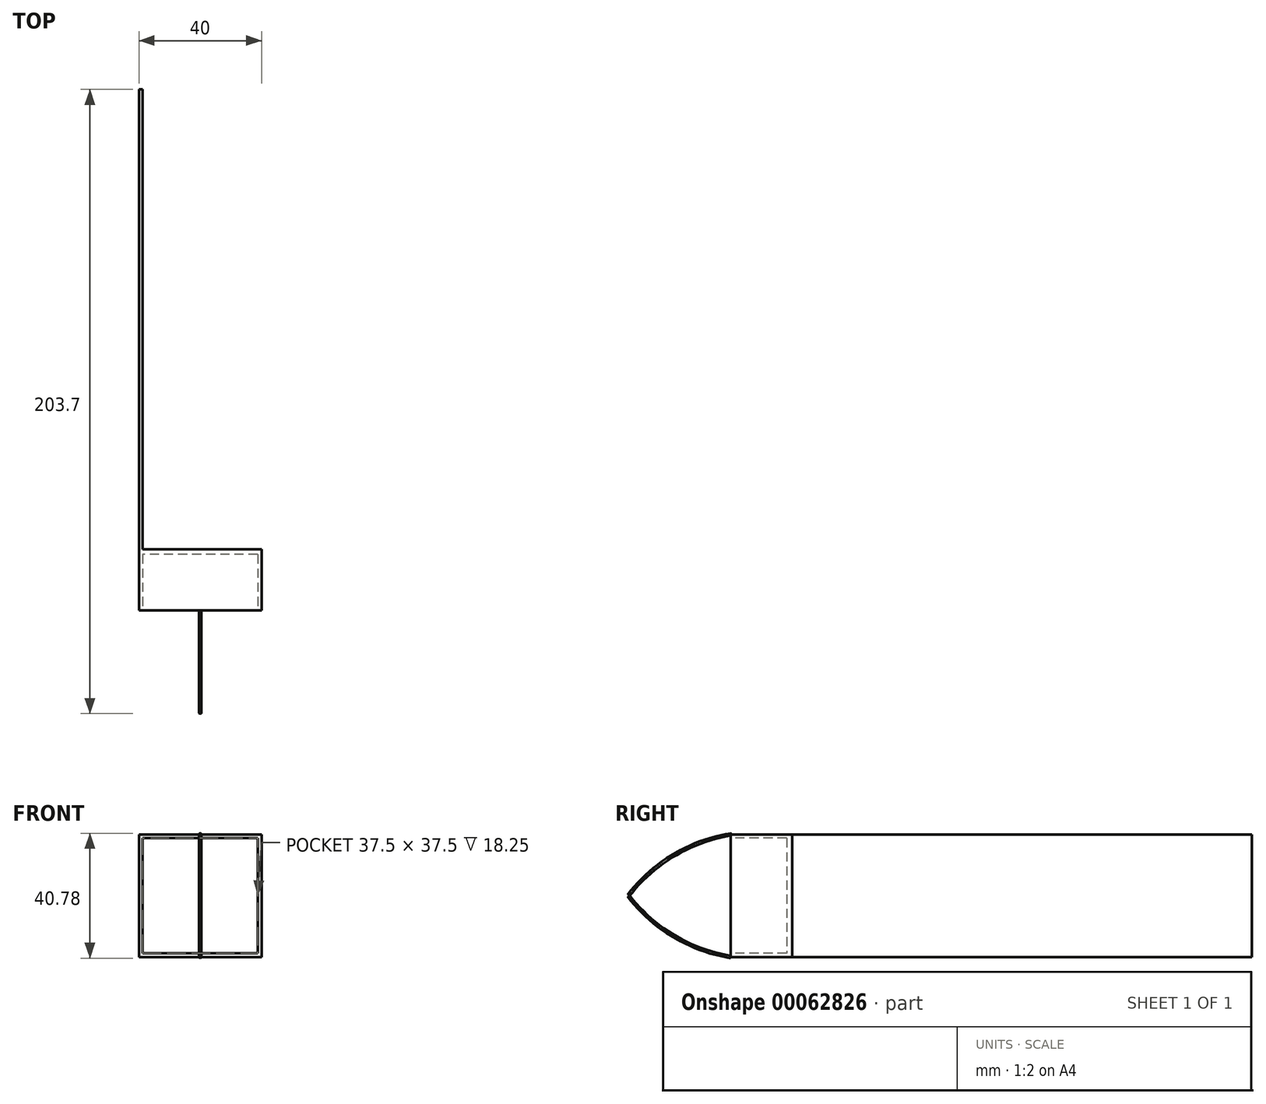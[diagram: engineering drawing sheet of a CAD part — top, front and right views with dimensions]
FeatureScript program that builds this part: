
annotation { "Feature Type Name" : "Feature", "Feature Type Description" : "" }
export const myFeature = defineFeature(function(context is Context, id is Id, definition is map)
    precondition{}
    {
        {
            var Q0;
            Q0=qCreatedBy(makeId("Front.planeOp"),FACE);
            var sketch = newSketch(context, id + "F0", { "sketchPlane" : qUnion([Q0])});
            skLineSegment(sketch, "E0.rect.bottom", {"start": v(20, 20) * mm, "end": v(-20, 20) * mm});
            skLineSegment(sketch, "E0.rect.top", {"start": v(20, -20) * mm, "end": v(-20, -20) * mm});
            skLineSegment(sketch, "E0.rect.left", {"start": v(20, 20) * mm, "end": v(20, -20) * mm});
            skLineSegment(sketch, "E0.rect.right", {"start": v(-20, 20) * mm, "end": v(-20, -20) * mm});
            skPoint(sketch, "E0.rect.middle", {"position": v(0, 0) * mm});
            skSolve(sketch);
        }
        {
            var Q0;
            Q0 = qSketchRegion(id + "F0", true);
            extrude(context, id + "F1", {"entities" : qUnion([Q0]), "depth" : 20 * mm});
        }
        {
            var Q0;
            Q0=makeQuery(id+"F1.opExtrude","CAP_FACE",FACE,{"disambiguationData":[OSD([sQuery(id+"F0.wireOp",EDGE,"E0.rect.bottom"),sQuery(id+"F0.wireOp",EDGE,"E0.rect.top"),sQuery(id+"F0.wireOp",EDGE,"E0.rect.left"),sQuery(id+"F0.wireOp",EDGE,"E0.rect.right")])],"isStart":false});
            var sketch = newSketch(context, id + "F2", { "sketchPlane" : qUnion([Q0])});
            skLineSegment(sketch, "E1.rect.bottom", {"start": v(18.75, 18.75) * mm, "end": v(-18.75, 18.75) * mm});
            skLineSegment(sketch, "E1.rect.top", {"start": v(18.75, -18.75) * mm, "end": v(-18.75, -18.75) * mm});
            skLineSegment(sketch, "E1.rect.left", {"start": v(18.75, 18.75) * mm, "end": v(18.75, -18.75) * mm});
            skLineSegment(sketch, "E1.rect.right", {"start": v(-18.75, 18.75) * mm, "end": v(-18.75, -18.75) * mm});
            skPoint(sketch, "E1.rect.middle", {"position": v(0, 0) * mm});
            skSolve(sketch);
        }
        {
            var Q0;
            Q0 = qSketchRegion(id + "F2", true);
            extrude(context, id + "F3", {"entities" : qUnion([Q0]), "operationType" : NewBodyOperationType.REMOVE, "oppositeDirection" : true, "depth" : 18.25 * mm});
        }
        {
            var Q0;
            Q0=makeQuery(id+"F1.opExtrude","CAP_FACE",FACE,{"disambiguationData":[OSD([sQuery(id+"F0.wireOp",EDGE,"E0.rect.bottom"),sQuery(id+"F0.wireOp",EDGE,"E0.rect.top"),sQuery(id+"F0.wireOp",EDGE,"E0.rect.left"),sQuery(id+"F0.wireOp",EDGE,"E0.rect.right")])],"isStart":true});
            var sketch = newSketch(context, id + "F4", { "sketchPlane" : qUnion([Q0])});
            skLineSegment(sketch, "E2", {"start": v(20, 12.78) * mm, "end": v(20, 10.03) * mm, "construction": true});
            skLineSegment(sketch, "E3.bottom", {"start": v(20, 20) * mm, "end": v(18.75, 20) * mm});
            skLineSegment(sketch, "E3.top", {"start": v(20, -20) * mm, "end": v(18.75, -20) * mm});
            skLineSegment(sketch, "E3.left", {"start": v(20, 20) * mm, "end": v(20, -20) * mm});
            skLineSegment(sketch, "E3.right", {"start": v(18.75, 20) * mm, "end": v(18.75, -20) * mm});
            skSolve(sketch);
        }
        {
            var Q0;
            Q0 = qSketchRegion(id + "F4", true);
            extrude(context, id + "F5", {"entities" : qUnion([Q0]), "operationType" : NewBodyOperationType.ADD, "depth" : 150 * mm});
        }
        {
            var Q0;
            Q0=qCreatedBy(makeId("Right.planeOp"),FACE);
            var sketch = newSketch(context, id + "F6", { "sketchPlane" : qUnion([Q0])});
            skArc(sketch, "E4", {"start": v(-53.66, 0) * mm, "mid": v(-38.84, -13.3) * mm, "end": v(-20.16, -20.16) * mm});
            skLineSegment(sketch, "E5", {"start": v(-74.12, 0) * mm, "end": v(-32.52, 0) * mm, "construction": true});
            skSolve(sketch);
        }
        {
            var Q0;
            Q0=makeQuery(id+"F1.opExtrude","CAP_FACE",FACE,{"disambiguationData":[OSD([sQuery(id+"F0.wireOp",EDGE,"E0.rect.bottom"),sQuery(id+"F0.wireOp",EDGE,"E0.rect.top"),sQuery(id+"F0.wireOp",EDGE,"E0.rect.left"),sQuery(id+"F0.wireOp",EDGE,"E0.rect.right")])],"isStart":false});
            var sketch = newSketch(context, id + "F7", { "sketchPlane" : qUnion([Q0])});
            skCircle(sketch, "E6", {"center": v(0, -20) * mm, "radius": 0.39 * mm});
            skSolve(sketch);
        }
        {
            var Q0;
            Q0 = qSketchRegion(id + "F7", true);
            var Q1;
            Q1 = qConstructionFilter(qBodyType(qCreatedBy(id + "F6" ,EDGE), BodyType.WIRE), ConstructionObject.NO);
            sweep(context, id + "F8", {"profiles" : qUnion([Q0]), "path" : qUnion([Q1])});
        }
        {
            var Q0;
            Q0=makeQuery(id+"F8.opSweep","SWEPT_BODY",BODY,{"disambiguationData":[OSD([sQuery(id+"F6.wireOp",EDGE,"E4"),sQuery(id+"F7.wireOp",EDGE,"E6")])]});
            var Q1;
            Q1=qCreatedBy(makeId("Top.planeOp"),FACE);
            mirror(context, id + "F9", {"entities" : qUnion([Q0]), "mirrorPlane" : qUnion([Q1])});
        }
    });
